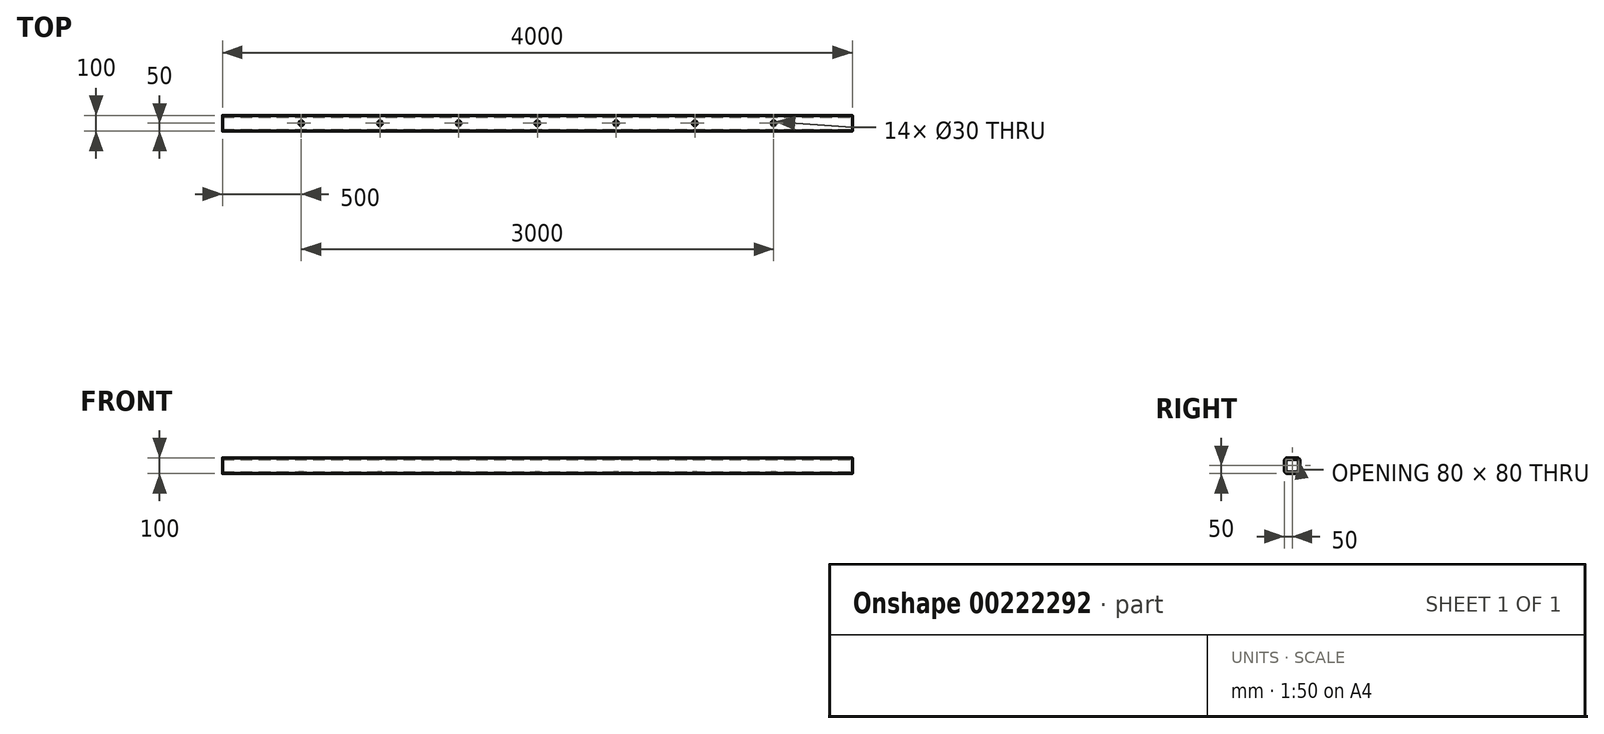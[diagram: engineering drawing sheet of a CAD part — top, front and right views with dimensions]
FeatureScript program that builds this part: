
annotation { "Feature Type Name" : "Feature", "Feature Type Description" : "" }
export const myFeature = defineFeature(function(context is Context, id is Id, definition is map)
    precondition{}
    {
        {
            var Q0;
            Q0=qCreatedBy(makeId("Top.planeOp"),FACE);
            var sketch = newSketch(context, id + "F0", { "sketchPlane" : qUnion([Q0])});
            skLineSegment(sketch, "E0.bottom", {"start": v(2000, 50) * mm, "end": v(-2000, 50) * mm});
            skLineSegment(sketch, "E0.top", {"start": v(2000, -50) * mm, "end": v(-2000, -50) * mm});
            skLineSegment(sketch, "E0.left", {"start": v(2000, 50) * mm, "end": v(2000, -50) * mm});
            skLineSegment(sketch, "E0.right", {"start": v(-2000, 50) * mm, "end": v(-2000, -50) * mm});
            skPoint(sketch, "E0.middle", {"position": v(0, 0) * mm});
            skSolve(sketch);
        }
        {
            var Q0;
            Q0 = qSketchRegion(id + "F0", true);
            extrude(context, id + "F1", {"entities" : qUnion([Q0]), "depth" : 100 * mm, "offsetDistance" : 25 * mm, "symmetric" : true});
        }
        {
            var Q0;
            Q0=makeQuery(id+"F1.opExtrude","CAP_EDGE",EDGE,{"disambiguationData":[OSD([sQuery(id+"F0.wireOp",EDGE,"E0.bottom")])],"isStart":false});
            var Q1;
            Q1=makeQuery(id+"F1.opExtrude","CAP_EDGE",EDGE,{"disambiguationData":[OSD([sQuery(id+"F0.wireOp",EDGE,"E0.top")])],"isStart":true});
            var Q2;
            Q2=makeQuery(id+"F1.opExtrude","CAP_EDGE",EDGE,{"disambiguationData":[OSD([sQuery(id+"F0.wireOp",EDGE,"E0.top")])],"isStart":false});
            var Q3;
            Q3=makeQuery(id+"F1.opExtrude","CAP_EDGE",EDGE,{"disambiguationData":[OSD([sQuery(id+"F0.wireOp",EDGE,"E0.bottom")])],"isStart":true});
            fillet(context, id + "F2", {"entities" : qUnion([Q0, Q1, Q2, Q3]), "radius" : 20 * mm, "tangentPropagation" : true, "allowEdgeOverflow" : false});
        }
        {
            var Q0;
            Q0=makeQuery(id+"F1.opExtrude","SWEPT_FACE",FACE,{"disambiguationData":[OSD([sQuery(id+"F0.wireOp",EDGE,"E0.left")])]});
            var Q1;
            Q1=makeQuery(id+"F1.opExtrude","SWEPT_FACE",FACE,{"disambiguationData":[OSD([sQuery(id+"F0.wireOp",EDGE,"E0.right")])]});
            shell(context, id + "F3", {"entities" : qUnion([Q0, Q1]), "thickness" : 10 * mm});
        }
        {
            var Q0;
            Q0=makeQuery(id+"F1.opExtrude","SWEPT_BODY",BODY,{"disambiguationData":[OSD([sQuery(id+"F0.wireOp",EDGE,"E0.bottom"),sQuery(id+"F0.wireOp",EDGE,"E0.top"),sQuery(id+"F0.wireOp",EDGE,"E0.left"),sQuery(id+"F0.wireOp",EDGE,"E0.right")])]});
            var Q1;
            Q1=qCreatedBy(makeId("Right.planeOp"),FACE);
            mirror(context, id + "F4", {"operationType" : NewBodyOperationType.ADD, "entities" : qUnion([Q0]), "mirrorPlane" : qUnion([Q1])});
        }
        {
            var Q0;
            Q0=qCreatedBy(makeId("Top.planeOp"),FACE);
            var sketch = newSketch(context, id + "F5", { "sketchPlane" : qUnion([Q0])});
            skCircle(sketch, "E1", {"center": v(0, 0) * mm, "radius": 15 * mm});
            skCircle(sketch, "E2.1.0.0", {"center": v(500, 0) * mm, "radius": 15 * mm});
            skCircle(sketch, "E2.2.0.0", {"center": v(1000, 0) * mm, "radius": 15 * mm});
            skLineSegment(sketch, "E2.direction1", {"start": v(0, 0) * mm, "end": v(500, 0) * mm, "construction": true});
            skCircle(sketch, "E3.0.3.0", {"center": v(1500, 0) * mm, "radius": 15 * mm});
            skCircle(sketch, "E4.1.0.0", {"center": v(-500, 0) * mm, "radius": 15 * mm});
            skCircle(sketch, "E4.2.0.0", {"center": v(-1000, 0) * mm, "radius": 15 * mm});
            skCircle(sketch, "E4.3.0.0", {"center": v(-1500, 0) * mm, "radius": 15 * mm});
            skLineSegment(sketch, "E4.direction1", {"start": v(0, 0) * mm, "end": v(-500, 0) * mm, "construction": true});
            skSolve(sketch);
        }
        {
            var Q0;
            Q0 = qSketchRegion(id + "F5", true);
            var Q1;
            Q1=sQuery(id+"F5.wireOp",EDGE,"E1");
            extrude(context, id + "F6", {"entities" : qUnion([Q0]), "operationType" : NewBodyOperationType.REMOVE, "surfaceEntities" : qUnion([Q1]), "oppositeDirection" : true, "depth" : 500 * mm, "offsetDistance" : 25 * mm, "symmetric" : true});
        }
    });
